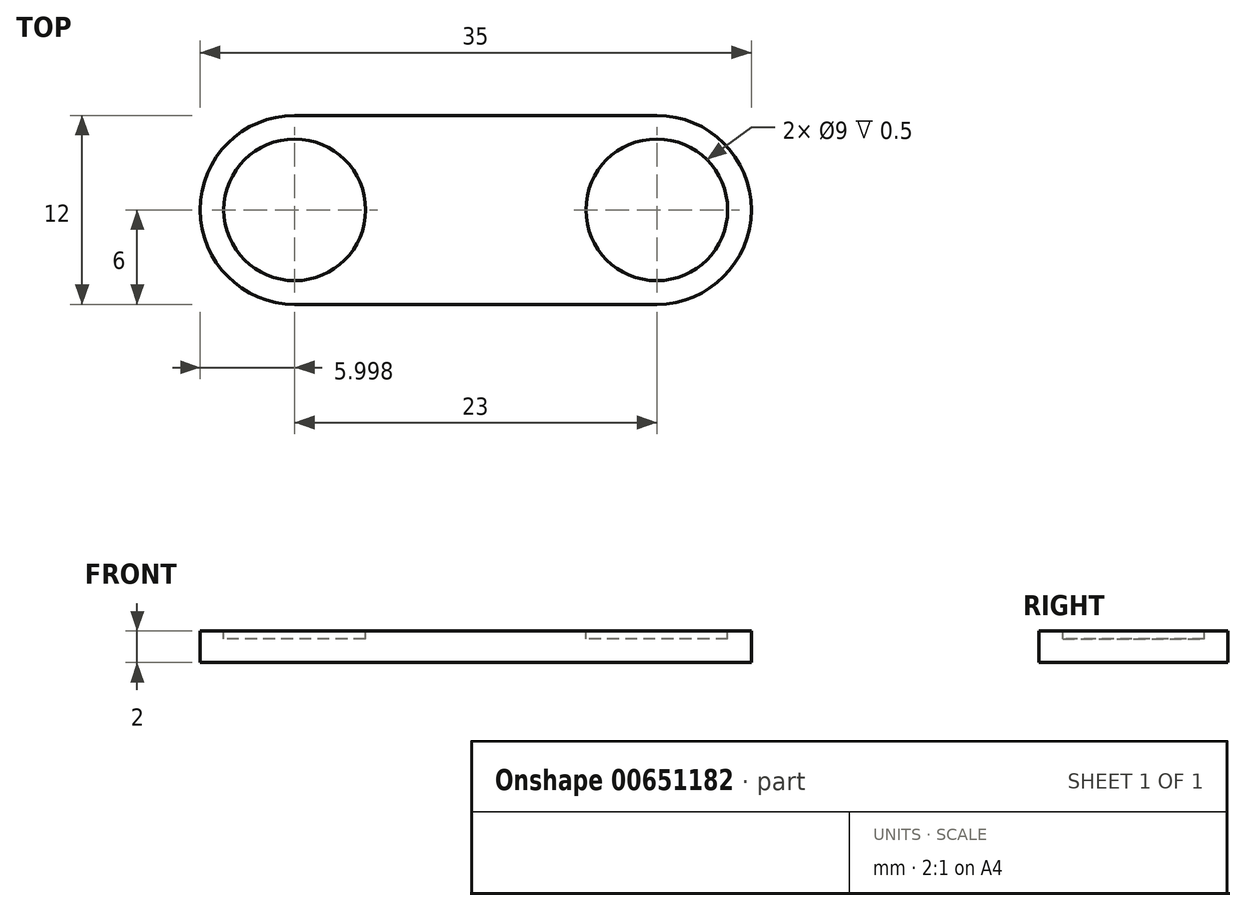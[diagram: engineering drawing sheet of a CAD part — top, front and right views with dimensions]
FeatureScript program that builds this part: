
annotation { "Feature Type Name" : "Feature", "Feature Type Description" : "" }
export const myFeature = defineFeature(function(context is Context, id is Id, definition is map)
    precondition{}
    {
        {
            var Q0;
            Q0=qCreatedBy(makeId("Top.planeOp"),FACE);
            var sketch = newSketch(context, id + "F0", { "sketchPlane" : qUnion([Q0])});
            skCircle(sketch, "E0", {"center": v(-49.73, 0) * mm, "radius": 6 * mm});
            skCircle(sketch, "E1", {"center": v(-26.73, 0) * mm, "radius": 6 * mm});
            skLineSegment(sketch, "E2", {"start": v(-49.73, 6) * mm, "end": v(-26.73, 6) * mm});
            skLineSegment(sketch, "E3", {"start": v(-26.73, -6) * mm, "end": v(-49.73, -6) * mm});
            skSolve(sketch);
        }
        {
            var Q0;
            Q0 = qSketchRegion(id + "F0", true);
            extrude(context, id + "F1", {"entities" : qUnion([Q0]), "depth" : 2 * mm, "offsetDistance" : 25 * mm});
        }
        {
            var Q0;
            Q0=makeQuery(id+"F1.opExtrude","CAP_FACE",FACE,{"disambiguationData":[OSD([sQuery(id+"F0.wireOp",EDGE,"E0"),sQuery(id+"F0.wireOp",EDGE,"E1"),sQuery(id+"F0.wireOp",EDGE,"E2"),sQuery(id+"F0.wireOp",EDGE,"E3")])],"isStart":false});
            var sketch = newSketch(context, id + "F2", { "sketchPlane" : qUnion([Q0])});
            skCircle(sketch, "E4", {"center": v(-49.73, 0) * mm, "radius": 4.5 * mm});
            skCircle(sketch, "E5", {"center": v(-26.73, 0) * mm, "radius": 4.5 * mm});
            skSolve(sketch);
        }
        {
            var Q0;
            Q0 = qSketchRegion(id + "F2", true);
            extrude(context, id + "F3", {"entities" : qUnion([Q0]), "operationType" : NewBodyOperationType.REMOVE, "oppositeDirection" : true, "depth" : 0.5 * mm, "offsetDistance" : 25 * mm});
        }
    });
